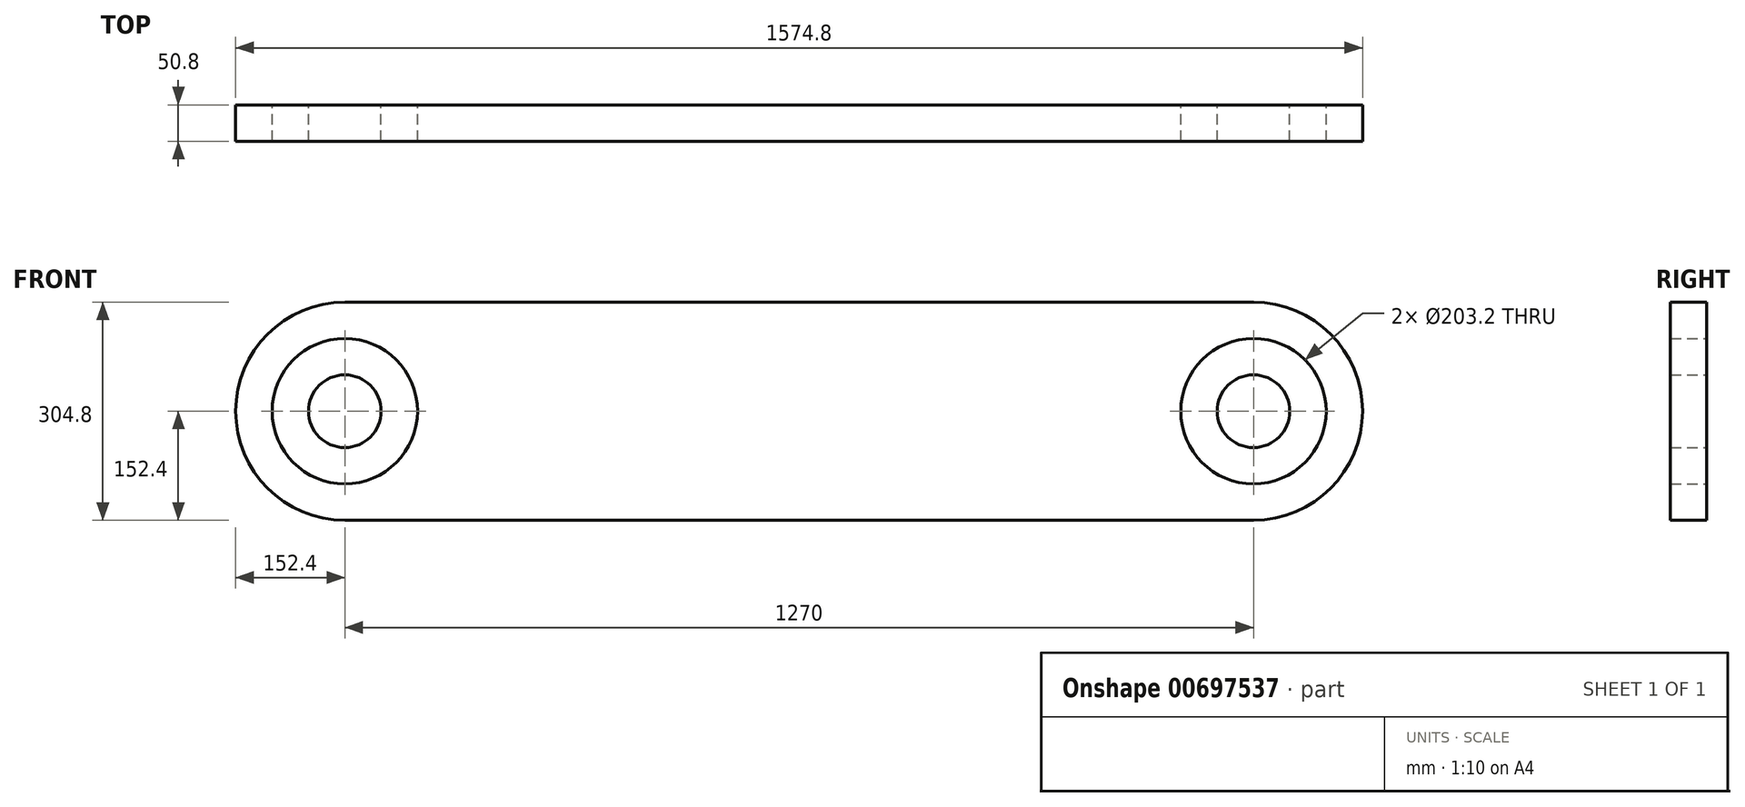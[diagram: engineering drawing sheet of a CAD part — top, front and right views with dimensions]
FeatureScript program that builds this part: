
annotation { "Feature Type Name" : "Feature", "Feature Type Description" : "" }
export const myFeature = defineFeature(function(context is Context, id is Id, definition is map)
    precondition{}
    {
        {
            var Q0;
            Q0=qCreatedBy(makeId("Front.planeOp"),FACE);
            var sketch = newSketch(context, id + "F0", { "sketchPlane" : qUnion([Q0])});
            skCircle(sketch, "E0", {"center": v(-635, 0) * mm, "radius": 101.6 * mm});
            skCircle(sketch, "E1", {"center": v(-635, 0) * mm, "radius": 50.8 * mm});
            skCircle(sketch, "E2", {"center": v(-635, 0) * mm, "radius": 152.4 * mm});
            skLineSegment(sketch, "E3", {"start": v(-635, 152.4) * mm, "end": v(0, 152.4) * mm});
            skLineSegment(sketch, "E4", {"start": v(0, 152.4) * mm, "end": v(0, -152.4) * mm});
            skLineSegment(sketch, "E5", {"start": v(0, -152.4) * mm, "end": v(-635, -152.4) * mm});
            skSolve(sketch);
        }
        {
            var Q0;
            Q0=makeQuery(id+"F0.imprint","IMPRINT",FACE,{"disambiguationData":[TD([[makeQuery(id+"F0.imprint","IMPRINT",EDGE,{"derivedFrom":sQuery(id+"F0.wireOp",EDGE,"E1")}),1.0]])]});
            var Q1;
            {var subQ0=sQuery(id+"F0.wireOp",EDGE,"E3");Q1=makeQuery(id+"F0.imprint","IMPRINT",FACE,{"disambiguationData":[TD([[makeQuery(id+"F0.imprint","IMPRINT",EDGE,{"derivedFrom":subQ0}),-1.0]])]});}
            var Q2;
            Q2=makeQuery(id+"F0.imprint","IMPRINT",FACE,{"disambiguationData":[TD([[makeQuery(id+"F0.imprint","IMPRINT",EDGE,{"derivedFrom":sQuery(id+"F0.wireOp",EDGE,"E0")}),-1.0]])]});
            extrude(context, id + "F1", {"entities" : qUnion([Q0, Q1, Q2]), "depth" : 50.8 * mm, "offsetDistance" : 25.4 * mm});
        }
        {
            var Q0;
            Q0=makeQuery(id+"F1.opExtrude","SWEPT_BODY",BODY,{"disambiguationData":[OSD([sQuery(id+"F0.wireOp",EDGE,"E0"),sQuery(id+"F0.wireOp",EDGE,"E2"),sQuery(id+"F0.wireOp",EDGE,"E3"),sQuery(id+"F0.wireOp",EDGE,"E4"),sQuery(id+"F0.wireOp",EDGE,"E5")])]});
            var Q1;
            Q1=makeQuery(id+"F1.opExtrude","SWEPT_BODY",BODY,{"disambiguationData":[OSD([sQuery(id+"F0.wireOp",EDGE,"E1")])]});
            var Q2;
            Q2=makeQuery(id+"F1.opExtrude","SWEPT_FACE",FACE,{"disambiguationData":[OSD([sQuery(id+"F0.wireOp",EDGE,"E4")])]});
            mirror(context, id + "F2", {"operationType" : NewBodyOperationType.ADD, "entities" : qUnion([Q0, Q1]), "mirrorPlane" : qUnion([Q2])});
        }
    });
